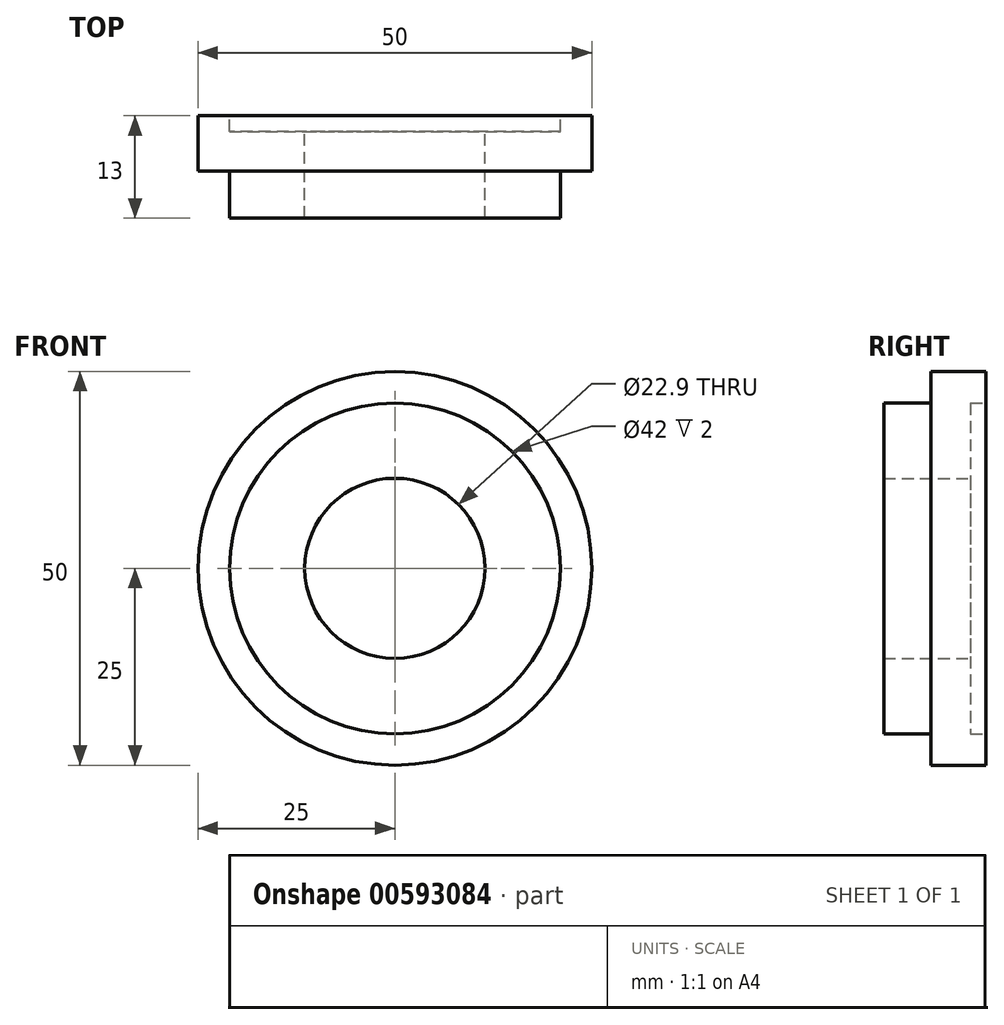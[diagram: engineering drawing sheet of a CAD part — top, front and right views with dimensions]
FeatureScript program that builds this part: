
annotation { "Feature Type Name" : "Feature", "Feature Type Description" : "" }
export const myFeature = defineFeature(function(context is Context, id is Id, definition is map)
    precondition{}
    {
        {
            var Q0;
            Q0=qCreatedBy(makeId("Front.planeOp"),FACE);
            var sketch = newSketch(context, id + "F0", { "sketchPlane" : qUnion([Q0])});
            skCircle(sketch, "E0", {"center": v(0, 0) * mm, "radius": 25 * mm});
            skCircle(sketch, "E1", {"center": v(0, 0) * mm, "radius": 11.45 * mm});
            skSolve(sketch);
        }
        {
            var Q0;
            Q0 = qSketchRegion(id + "F0", true);
            extrude(context, id + "F1", {"entities" : qUnion([Q0]), "depth" : 13 * mm, "offsetDistance" : 25 * mm});
        }
        {
            var Q0;
            Q0=makeQuery(id+"F1.opExtrude","CAP_FACE",FACE,{"disambiguationData":[OSD([sQuery(id+"F0.wireOp",EDGE,"E0"),sQuery(id+"F0.wireOp",EDGE,"E1")])],"isStart":false});
            var sketch = newSketch(context, id + "F2", { "sketchPlane" : qUnion([Q0])});
            skCircle(sketch, "E2", {"center": v(0, 0) * mm, "radius": 21 * mm});
            skSolve(sketch);
        }
        {
            var Q0;
            Q0=makeQuery(id+"F2.imprint","IMPRINT",FACE,{"disambiguationData":[TD([[makeQuery(id+"F2.imprint","IMPRINT",EDGE,{"derivedFrom":makeQuery(id+"F1.opExtrude","CAP_EDGE",EDGE,{"disambiguationData":[OSD([sQuery(id+"F0.wireOp",EDGE,"E1")])],"isStart":false})}),1.0]])]});
            var Q1;
            Q1=makeQuery(id+"F2.imprint","IMPRINT",FACE,{"disambiguationData":[TD([[makeQuery(id+"F2.imprint","IMPRINT",EDGE,{"derivedFrom":sQuery(id+"F2.wireOp",EDGE,"E2")}),-1.0]])]});
            extrude(context, id + "F3", {"entities" : qUnion([Q0, Q1]), "operationType" : NewBodyOperationType.REMOVE, "oppositeDirection" : true, "depth" : 6 * mm, "offsetDistance" : 25 * mm});
        }
        {
            var Q0;
            Q0=makeQuery(id+"F1.opExtrude","CAP_FACE",FACE,{"disambiguationData":[OSD([sQuery(id+"F0.wireOp",EDGE,"E0"),sQuery(id+"F0.wireOp",EDGE,"E1")])],"isStart":true});
            var sketch = newSketch(context, id + "F4", { "sketchPlane" : qUnion([Q0])});
            skCircle(sketch, "E3", {"center": v(0, 0) * mm, "radius": 21 * mm});
            skSolve(sketch);
        }
        {
            var Q0;
            Q0=makeQuery(id+"F4.imprint","IMPRINT",FACE,{"disambiguationData":[TD([[makeQuery(id+"F4.imprint","IMPRINT",EDGE,{"derivedFrom":makeQuery(id+"F1.opExtrude","CAP_EDGE",EDGE,{"disambiguationData":[OSD([sQuery(id+"F0.wireOp",EDGE,"E1")])],"isStart":true})}),-1.0]])]});
            var Q1;
            Q1=makeQuery(id+"F4.imprint","IMPRINT",FACE,{"disambiguationData":[TD([[makeQuery(id+"F4.imprint","IMPRINT",EDGE,{"derivedFrom":sQuery(id+"F4.wireOp",EDGE,"E3")}),1.0]])]});
            extrude(context, id + "F5", {"entities" : qUnion([Q0, Q1]), "operationType" : NewBodyOperationType.REMOVE, "oppositeDirection" : true, "depth" : 2 * mm, "offsetDistance" : 25 * mm});
        }
    });
